# Revit family: Haworth_Masters_Desk_KeystoneFull
name_source: partatom
category: Furniture Systems
revit_build: Autodesk Revit 2018 (Build: 20170223_1515(x64)
units: mm (PartAtom-declared; Revit-internal decimal feet)

## family parameters
Always vertical = Yes
Cut with Voids When Loaded = No
OmniClass Number = 23.40.70.14.64.21
OmniClass Title = Systems Furniture
Part Type = Normal
Room Calculation Point = No
Round Connector Dimension = Use Diameter
Shared = No
Work Plane-Based = No

## types (1)
- 48d 60w
    Actual Depth Large = 48"
    Actual Height = 29 1/8"
    Actual Width = 60"
    Assembly Code = E2020200
    Column Support = Yes
    Custom Size = No
    Depth Large = 48"
    Depth Small Offset = 6 1/2"
    Description = Haworth - Masters Desk - Keystone - Full
    Edge Finish = Haworth _ Wood _ White Oak
    Manufacturer = Haworth
    Max. Depth = 48"
    Max. Width = 72"
    Min. Depth = 42"
    Min. Width = 60"
    Model = Haworth - Masters Desk - Keystone - Full
    Post Finish = Haworth _ Paint _ Metallic Champagne
    Post Position = 18"
    Revision Number = 2
    Size = Verify Final Dim. w/ Haworth
    Stanchions = Yes
    Standard Sizes = 48x60 in.
    Support Height = 22 3/4"
    Support Position = 13"
    Support Position Left = 24"
    Support Position Right = 12"
    Sustainability Info = http://www.haworth.com
    URL = www.haworth.com
    URL - Product = http://www.haworth.com
    Warranty = http://www.haworth.com
    Width = 60"
    Worksurface Finish = Haworth _ Wood _ White Oak

## geometry (parser evidence)
native form markers: Sweep x5
no freeform markers — native parametric forms only
